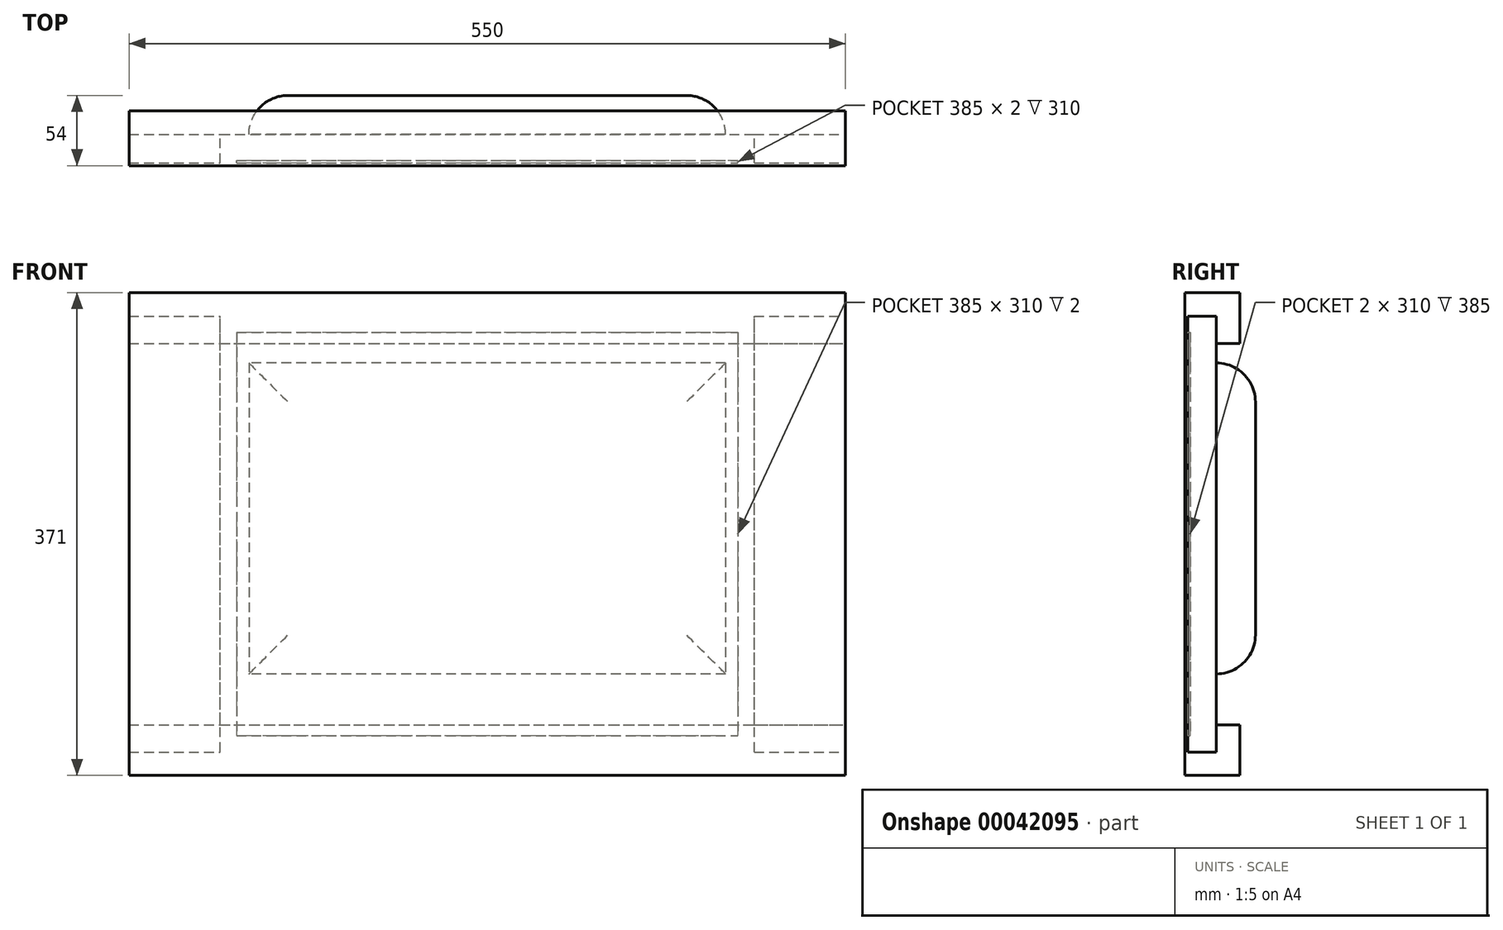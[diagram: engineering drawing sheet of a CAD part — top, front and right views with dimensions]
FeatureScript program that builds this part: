
annotation { "Feature Type Name" : "Feature", "Feature Type Description" : "" }
export const myFeature = defineFeature(function(context is Context, id is Id, definition is map)
    precondition{}
    {
        {
            var Q0;
            Q0=qCreatedBy(makeId("Front.planeOp"),FACE);
            var sketch = newSketch(context, id + "F0", { "sketchPlane" : qUnion([Q0])});
            skLineSegment(sketch, "E0.rect.bottom", {"start": v(205, -167.5) * mm, "end": v(-205, -167.5) * mm});
            skLineSegment(sketch, "E0.rect.top", {"start": v(205, 167.5) * mm, "end": v(-205, 167.5) * mm});
            skLineSegment(sketch, "E0.rect.left", {"start": v(205, -167.5) * mm, "end": v(205, 167.5) * mm});
            skLineSegment(sketch, "E0.rect.right", {"start": v(-205, -167.5) * mm, "end": v(-205, 167.5) * mm});
            skPoint(sketch, "E0.rect.middle", {"position": v(0, 0) * mm});
            skLineSegment(sketch, "E1.bottom", {"start": v(-192.5, 155) * mm, "end": v(192.5, 155) * mm});
            skLineSegment(sketch, "E1.top", {"start": v(-192.5, -155) * mm, "end": v(192.5, -155) * mm});
            skLineSegment(sketch, "E1.left", {"start": v(-192.5, 155) * mm, "end": v(-192.5, -155) * mm});
            skLineSegment(sketch, "E1.right", {"start": v(192.5, 155) * mm, "end": v(192.5, -155) * mm});
            skSolve(sketch);
        }
        {
            var Q0;
            Q0 = qSketchRegion(id + "F0", true);
            extrude(context, id + "F1", {"entities" : qUnion([Q0]), "depth" : 22 * mm});
        }
        {
            var Q0;
            Q0=makeQuery(id+"F0.imprint","IMPRINT",FACE,{"disambiguationData":[TD([[makeQuery(id+"F0.imprint","IMPRINT",EDGE,{"derivedFrom":sQuery(id+"F0.wireOp",EDGE,"E1.bottom")}),-1.0]])]});
            extrude(context, id + "F2", {"entities" : qUnion([Q0]), "operationType" : NewBodyOperationType.ADD, "depth" : 20 * mm});
        }
        {
            var Q0;
            Q0=makeQuery(id+"F1.opExtrude","SWEPT_FACE",FACE,{"disambiguationData":[OSD([sQuery(id+"F0.wireOp",EDGE,"E0.rect.left")])]});
            var sketch = newSketch(context, id + "F3", { "sketchPlane" : qUnion([Q0])});
            skLineSegment(sketch, "E2", {"start": v(-22, -167.5) * mm, "end": v(-22, -185.5) * mm});
            skLineSegment(sketch, "E3", {"start": v(-22, -185.5) * mm, "end": v(18, -185.5) * mm});
            skLineSegment(sketch, "E4", {"start": v(18, -185.5) * mm, "end": v(18, -146.5) * mm});
            skLineSegment(sketch, "E5", {"start": v(18, -146.5) * mm, "end": v(0, -146.5) * mm});
            skLineSegment(sketch, "E6", {"start": v(0, -146.5) * mm, "end": v(0, -167.5) * mm});
            skLineSegment(sketch, "E7", {"start": v(0, -167.5) * mm, "end": v(-22, -167.5) * mm});
            skLineSegment(sketch, "E8.MirrorCS", {"start": v(18, 146.5) * mm, "end": v(0, 146.5) * mm});
            skLineSegment(sketch, "E9.MirrorCS", {"start": v(18, 185.5) * mm, "end": v(18, 146.5) * mm});
            skLineSegment(sketch, "E10.MirrorCS", {"start": v(0, 146.5) * mm, "end": v(0, 167.5) * mm});
            skLineSegment(sketch, "E11.MirrorCS", {"start": v(0, 167.5) * mm, "end": v(-22, 167.5) * mm});
            skLineSegment(sketch, "E12.MirrorCS", {"start": v(-22, 167.5) * mm, "end": v(-22, 185.5) * mm});
            skLineSegment(sketch, "E13.MirrorCS", {"start": v(-22, 185.5) * mm, "end": v(18, 185.5) * mm});
            skSolve(sketch);
        }
        {
            var Q0;
            Q0 = qSketchRegion(id + "F3", true);
            var Q1;
            Q1=makeQuery(id+"F1.opExtrude","SWEPT_FACE",FACE,{"disambiguationData":[OSD([sQuery(id+"F0.wireOp",EDGE,"E0.rect.right")])]});
            extrude(context, id + "F4", {"entities" : qUnion([Q0]), "oppositeDirection" : true, "endBoundEntityFace" : qUnion([Q1]), "depth" : 480 * mm, "hasSecondDirection" : true, "secondDirectionOppositeDirection" : false, "secondDirectionDepth" : 70 * mm});
        }
        {
            var Q0;
            {var subQ0=sQuery(id+"F0.wireOp",EDGE,"E1.bottom");var subQ1=sQuery(id+"F0.wireOp",EDGE,"E1.top");var subQ2=sQuery(id+"F0.wireOp",EDGE,"E1.left");var subQ3=sQuery(id+"F0.wireOp",EDGE,"E1.right");Q0=makeQuery(id+"F2.boolean.opBoolean","MERGE",FACE,{"derivedFrom":[makeQuery(id+"F1.opExtrude","CAP_FACE",FACE,{"disambiguationData":[OSD([sQuery(id+"F0.wireOp",EDGE,"E0.rect.bottom"),sQuery(id+"F0.wireOp",EDGE,"E0.rect.top"),sQuery(id+"F0.wireOp",EDGE,"E0.rect.left"),sQuery(id+"F0.wireOp",EDGE,"E0.rect.right"),subQ0,subQ1,subQ2,subQ3])],"isStart":true}),makeQuery(id+"F2.opExtrude","CAP_FACE",FACE,{"disambiguationData":[OSD([subQ0,subQ1,subQ2,subQ3])],"isStart":true})]});}
            var sketch = newSketch(context, id + "F5", { "sketchPlane" : qUnion([Q0])});
            skLineSegment(sketch, "E14.bottom", {"start": v(-183, 131.5) * mm, "end": v(183, 131.5) * mm});
            skLineSegment(sketch, "E14.top", {"start": v(-183, -107.5) * mm, "end": v(183, -107.5) * mm});
            skLineSegment(sketch, "E14.left", {"start": v(-183, 131.5) * mm, "end": v(-183, -107.5) * mm});
            skLineSegment(sketch, "E14.right", {"start": v(183, 131.5) * mm, "end": v(183, -107.5) * mm});
            skSolve(sketch);
        }
        {
            var Q0;
            Q0=makeQuery(id+"F5.imprint","IMPRINT",FACE,{"disambiguationData":[TD([[makeQuery(id+"F5.imprint","IMPRINT",EDGE,{"derivedFrom":sQuery(id+"F5.wireOp",EDGE,"E14.bottom")}),-1.0]])]});
            extrude(context, id + "F6", {"entities" : qUnion([Q0]), "operationType" : NewBodyOperationType.ADD, "depth" : 30 * mm});
        }
        {
            var Q0;
            Q0=makeQuery(id+"F6.opExtrude","CAP_EDGE",EDGE,{"disambiguationData":[OSD([sQuery(id+"F5.wireOp",EDGE,"E14.right")])],"isStart":false});
            var Q1;
            Q1=makeQuery(id+"F6.opExtrude","CAP_EDGE",EDGE,{"disambiguationData":[OSD([sQuery(id+"F5.wireOp",EDGE,"E14.bottom")])],"isStart":false});
            var Q2;
            Q2=makeQuery(id+"F6.opExtrude","CAP_EDGE",EDGE,{"disambiguationData":[OSD([sQuery(id+"F5.wireOp",EDGE,"E14.left")])],"isStart":false});
            var Q3;
            Q3=makeQuery(id+"F6.opExtrude","CAP_EDGE",EDGE,{"disambiguationData":[OSD([sQuery(id+"F5.wireOp",EDGE,"E14.top")])],"isStart":false});
            fillet(context, id + "F7", {"entities" : qUnion([Q0, Q1, Q2, Q3]), "radius" : 30 * mm, "tangentPropagation" : true, "allowEdgeOverflow" : false});
        }
        {
            var Q0;
            Q0=makeQuery(id+"F4.opExtrude","SWEPT_BODY",BODY,{"disambiguationData":[OSD([sQuery(id+"F3.wireOp",EDGE,"E2"),sQuery(id+"F3.wireOp",EDGE,"E3"),sQuery(id+"F3.wireOp",EDGE,"E4"),sQuery(id+"F3.wireOp",EDGE,"E5"),sQuery(id+"F3.wireOp",EDGE,"E6"),sQuery(id+"F3.wireOp",EDGE,"E7")])]});
            var Q1;
            Q1=makeQuery(id+"F4.opExtrude","SWEPT_BODY",BODY,{"disambiguationData":[OSD([sQuery(id+"F3.wireOp",EDGE,"E8.MirrorCS"),sQuery(id+"F3.wireOp",EDGE,"E9.MirrorCS"),sQuery(id+"F3.wireOp",EDGE,"E10.MirrorCS"),sQuery(id+"F3.wireOp",EDGE,"E11.MirrorCS"),sQuery(id+"F3.wireOp",EDGE,"E12.MirrorCS"),sQuery(id+"F3.wireOp",EDGE,"E13.MirrorCS")])]});
            var Q2;
            Q2=makeQuery(id+"F1.opExtrude","SWEPT_BODY",BODY,{"disambiguationData":[OSD([sQuery(id+"F0.wireOp",EDGE,"E0.rect.bottom"),sQuery(id+"F0.wireOp",EDGE,"E0.rect.top"),sQuery(id+"F0.wireOp",EDGE,"E0.rect.left"),sQuery(id+"F0.wireOp",EDGE,"E0.rect.right"),sQuery(id+"F0.wireOp",EDGE,"E1.bottom"),sQuery(id+"F0.wireOp",EDGE,"E1.top"),sQuery(id+"F0.wireOp",EDGE,"E1.left"),sQuery(id+"F0.wireOp",EDGE,"E1.right")])]});
            booleanBodies(context, id + "F8", {"operationType" : BooleanOperationType.UNION, "tools" : qUnion([Q0, Q1, Q2])});
        }
        {
            var Q0;
            Q0=makeQuery(id+"F8.opBoolean","MERGE",FACE,{"derivedFrom":[makeQuery(id+"F1.opExtrude","CAP_FACE",FACE,{"disambiguationData":[OSD([sQuery(id+"F0.wireOp",EDGE,"E0.rect.bottom"),sQuery(id+"F0.wireOp",EDGE,"E0.rect.top"),sQuery(id+"F0.wireOp",EDGE,"E0.rect.left"),sQuery(id+"F0.wireOp",EDGE,"E0.rect.right"),sQuery(id+"F0.wireOp",EDGE,"E1.bottom"),sQuery(id+"F0.wireOp",EDGE,"E1.top"),sQuery(id+"F0.wireOp",EDGE,"E1.left"),sQuery(id+"F0.wireOp",EDGE,"E1.right")])],"isStart":false}),makeQuery(id+"F4.opExtrude","SWEPT_FACE",FACE,{"disambiguationData":[OSD([sQuery(id+"F3.wireOp",EDGE,"E2")])]}),makeQuery(id+"F4.opExtrude","SWEPT_FACE",FACE,{"disambiguationData":[OSD([sQuery(id+"F3.wireOp",EDGE,"E12.MirrorCS")])]})]});
            var sketch = newSketch(context, id + "F9", { "sketchPlane" : qUnion([Q0])});
            skLineSegment(sketch, "E15.bottom", {"start": v(-275, 185.5) * mm, "end": v(275, 185.5) * mm});
            skLineSegment(sketch, "E15.top", {"start": v(-275, -185.5) * mm, "end": v(275, -185.5) * mm});
            skLineSegment(sketch, "E15.left", {"start": v(-275, 185.5) * mm, "end": v(-275, -185.5) * mm});
            skLineSegment(sketch, "E15.right", {"start": v(275, 185.5) * mm, "end": v(275, -185.5) * mm});
            skSolve(sketch);
        }
        {
            var Q0;
            Q0 = qSketchRegion(id + "F9", true);
            extrude(context, id + "F10", {"entities" : qUnion([Q0]), "operationType" : NewBodyOperationType.ADD, "depth" : 2 * mm});
        }
    });
